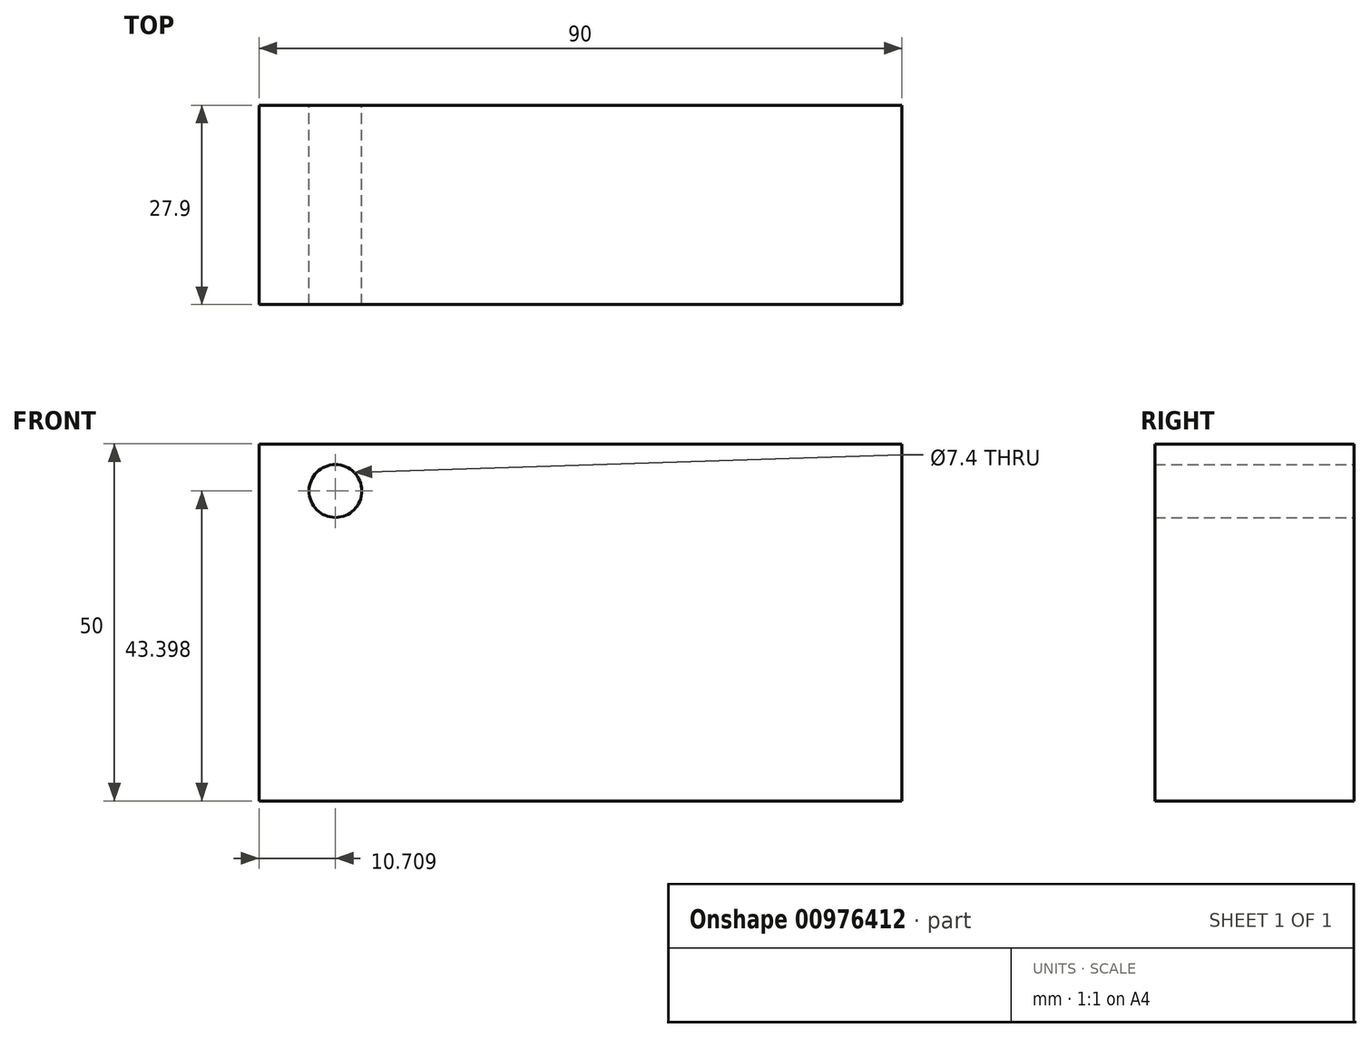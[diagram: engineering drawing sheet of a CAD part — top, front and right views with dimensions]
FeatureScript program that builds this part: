
annotation { "Feature Type Name" : "Feature", "Feature Type Description" : "" }
export const myFeature = defineFeature(function(context is Context, id is Id, definition is map)
    precondition{}
    {
        {
            var Q0;
            Q0=qCreatedBy(makeId("Front.planeOp"),FACE);
            var sketch = newSketch(context, id + "F0", { "sketchPlane" : qUnion([Q0])});
            skLineSegment(sketch, "E0.bottom", {"start": v(-43.56, 25.03) * mm, "end": v(46.44, 25.03) * mm});
            skLineSegment(sketch, "E0.top", {"start": v(-43.56, -24.97) * mm, "end": v(46.44, -24.97) * mm});
            skLineSegment(sketch, "E0.left", {"start": v(-43.56, 25.03) * mm, "end": v(-43.56, -24.97) * mm});
            skLineSegment(sketch, "E0.right", {"start": v(46.44, 25.03) * mm, "end": v(46.44, -24.97) * mm});
            skSolve(sketch);
        }
        {
            var Q0;
            Q0=makeQuery(id+"F0.imprint","IMPRINT",FACE,{"disambiguationData":[TD([[makeQuery(id+"F0.imprint","IMPRINT",EDGE,{"derivedFrom":sQuery(id+"F0.wireOp",EDGE,"E0.bottom")}),-1.0]])]});
            extrude(context, id + "F1", {"entities" : qUnion([Q0]), "depth" : 27.9 * mm, "offsetDistance" : 25 * mm});
        }
        {
            var Q0;
            Q0=qCreatedBy(makeId("Front.planeOp"),FACE);
            var sketch = newSketch(context, id + "F2", { "sketchPlane" : qUnion([Q0])});
            skCircle(sketch, "E1", {"center": v(-32.85, 18.43) * mm, "radius": 3.7 * mm});
            skCircle(sketch, "E2", {"center": v(-33.87, 5.69) * mm, "radius": 4.22 * mm});
            skSolve(sketch);
        }
        {
            var Q0;
            Q0=makeQuery(id+"F2.imprint","IMPRINT",FACE,{"disambiguationData":[TD([[makeQuery(id+"F2.imprint","IMPRINT",EDGE,{"derivedFrom":sQuery(id+"F2.wireOp",EDGE,"E1")}),1.0]])]});
            extrude(context, id + "F3", {"entities" : qUnion([Q0]), "operationType" : NewBodyOperationType.REMOVE, "depth" : 28.9 * mm, "offsetDistance" : 25 * mm});
        }
    });
